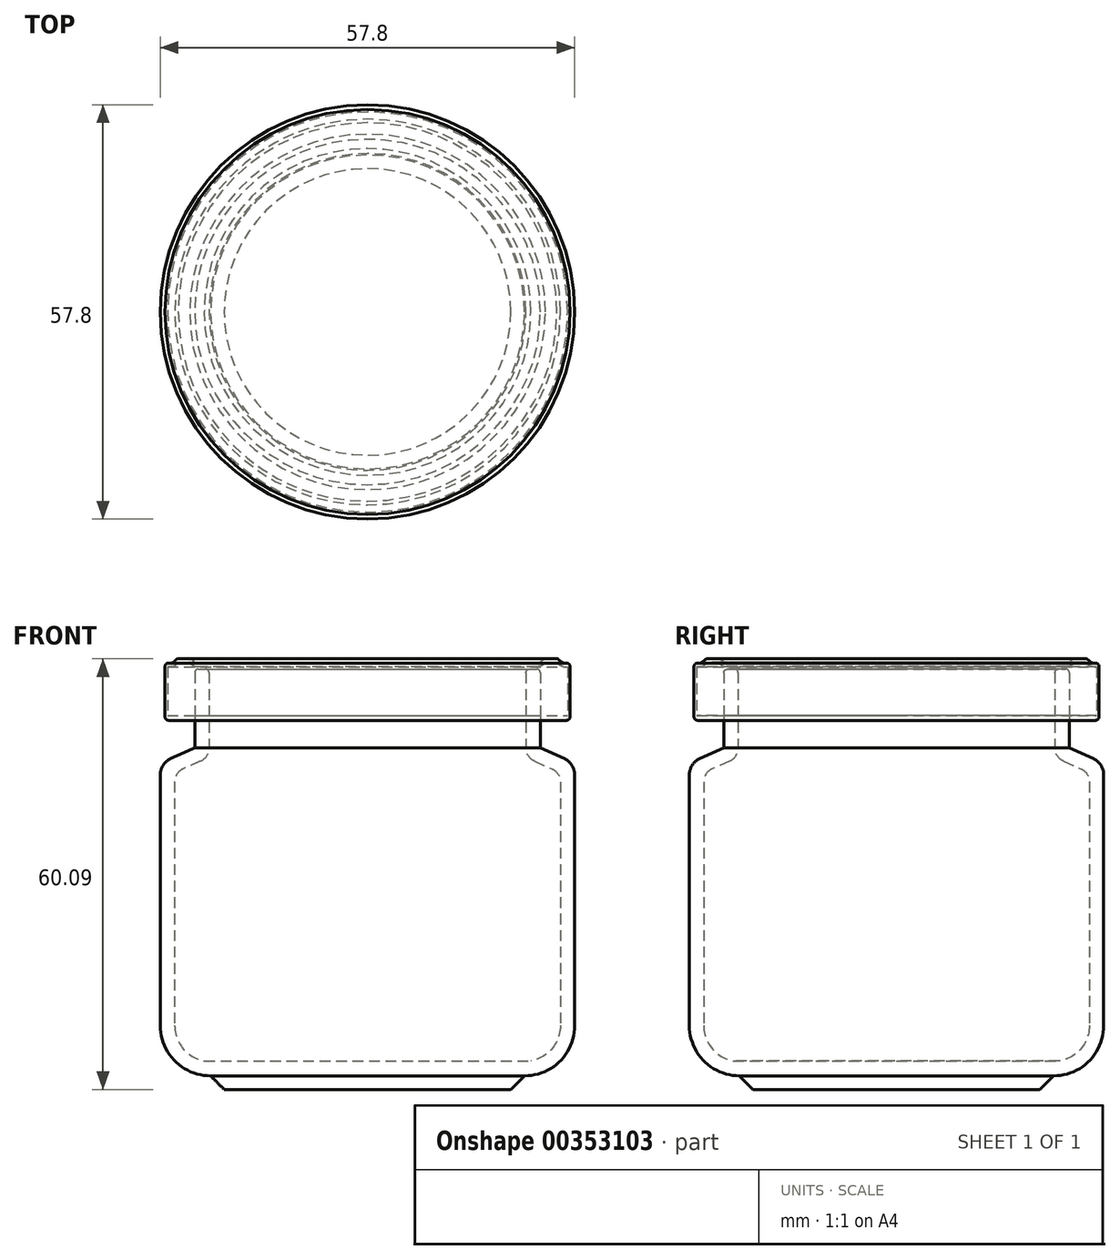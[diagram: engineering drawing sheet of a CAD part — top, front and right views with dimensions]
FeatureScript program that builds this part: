
annotation { "Feature Type Name" : "Feature", "Feature Type Description" : "" }
export const myFeature = defineFeature(function(context is Context, id is Id, definition is map)
    precondition{}
    {
        {
            var Q0;
            Q0=qCreatedBy(makeId("Front.planeOp"),FACE);
            var sketch = newSketch(context, id + "F0", { "sketchPlane" : qUnion([Q0])});
            skLineSegment(sketch, "E0", {"start": v(0, 0) * mm, "end": v(20, 0) * mm});
            skLineSegment(sketch, "E1", {"start": v(20, 0) * mm, "end": v(21.9, 1.9) * mm});
            skArc(sketch, "E2", {"start": v(21.9, 1.9) * mm, "mid": v(26.85, 3.95) * mm, "end": v(28.9, 8.9) * mm});
            skLineSegment(sketch, "E3", {"start": v(28.9, 8.9) * mm, "end": v(28.9, 43.9) * mm});
            skArc(sketch, "E4", {"start": v(28.9, 43.9) * mm, "mid": v(28.5, 45.26) * mm, "end": v(27.41, 46.19) * mm});
            skLineSegment(sketch, "E5", {"start": v(27.41, 46.19) * mm, "end": v(24.1, 47.65) * mm});
            skLineSegment(sketch, "E6", {"start": v(24.1, 47.65) * mm, "end": v(24.1, 58.15) * mm});
            skLineSegment(sketch, "E7.0", {"start": v(22.1, 47.65) * mm, "end": v(22.1, 58.15) * mm});
            skLineSegment(sketch, "E7.1", {"start": v(25.7, 44.75) * mm, "end": v(23.3, 45.82) * mm});
            skLineSegment(sketch, "E7.2", {"start": v(26.9, 8.9) * mm, "end": v(26.9, 42.92) * mm});
            skLineSegment(sketch, "E8", {"start": v(22.6, 58.65) * mm, "end": v(23.6, 58.65) * mm});
            skPoint(sketch, "E9.visualSharp", {"position": v(22.1, 58.65) * mm});
            skArc(sketch, "E9.filletArc", {"start": v(22.6, 58.65) * mm, "mid": v(22.25, 58.5) * mm, "end": v(22.1, 58.15) * mm});
            skPoint(sketch, "E10.visualSharp", {"position": v(24.1, 58.65) * mm});
            skArc(sketch, "E10.filletArc", {"start": v(24.1, 58.15) * mm, "mid": v(23.95, 58.5) * mm, "end": v(23.6, 58.65) * mm});
            skPoint(sketch, "E11.visualSharp", {"position": v(22.1, 46.35) * mm});
            skArc(sketch, "E11.filletArc", {"start": v(22.1, 47.65) * mm, "mid": v(22.42, 46.56) * mm, "end": v(23.3, 45.82) * mm});
            skPoint(sketch, "E12.visualSharp", {"position": v(26.9, 44.23) * mm});
            skArc(sketch, "E12.filletArc", {"start": v(26.9, 42.92) * mm, "mid": v(26.58, 44.01) * mm, "end": v(25.7, 44.75) * mm});
            skPoint(sketch, "E13.visualSharp", {"position": v(26.9, -0.68) * mm});
            skArc(sketch, "E13.filletArc", {"start": v(22.78, 3.98) * mm, "mid": v(25.73, 5.7) * mm, "end": v(26.9, 8.9) * mm});
            skLineSegment(sketch, "E14", {"start": v(22.78, 3.98) * mm, "end": v(0, 3.98) * mm});
            skLineSegment(sketch, "E15", {"start": v(0, 0) * mm, "end": v(0, 55.91) * mm, "construction": true});
            skLineSegment(sketch, "E16", {"start": v(0, 3.98) * mm, "end": v(0, 0) * mm});
            skSolve(sketch);
        }
        {
            var Q0;
            Q0=qCreatedBy(makeId("Front.planeOp"),FACE);
            var sketch = newSketch(context, id + "F1", { "sketchPlane" : qUnion([Q0])});
            skLineSegment(sketch, "E17", {"start": v(24.1, 51.5) * mm, "end": v(27.75, 51.5) * mm});
            skLineSegment(sketch, "E18", {"start": v(28.25, 52) * mm, "end": v(28.25, 59) * mm});
            skLineSegment(sketch, "E19", {"start": v(27.75, 59.5) * mm, "end": v(27.4, 59.5) * mm});
            skLineSegment(sketch, "E20", {"start": v(27.05, 59.65) * mm, "end": v(26.75, 59.95) * mm});
            skLineSegment(sketch, "E21", {"start": v(26.4, 60.1) * mm, "end": v(24.81, 60.1) * mm});
            skLineSegment(sketch, "E22", {"start": v(24.46, 59.95) * mm, "end": v(24.16, 59.65) * mm});
            skLineSegment(sketch, "E23", {"start": v(23.8, 59.5) * mm, "end": v(0, 59.5) * mm});
            skPoint(sketch, "E24.visualSharp", {"position": v(24.01, 59.5) * mm});
            skArc(sketch, "E24.filletArc", {"start": v(23.8, 59.5) * mm, "mid": v(24, 59.54) * mm, "end": v(24.16, 59.65) * mm});
            skPoint(sketch, "E25.visualSharp", {"position": v(24.6, 60.1) * mm});
            skArc(sketch, "E25.filletArc", {"start": v(24.81, 60.1) * mm, "mid": v(24.62, 60.05) * mm, "end": v(24.46, 59.95) * mm});
            skPoint(sketch, "E26.visualSharp", {"position": v(26.6, 60.1) * mm});
            skArc(sketch, "E26.filletArc", {"start": v(26.75, 59.95) * mm, "mid": v(26.59, 60.05) * mm, "end": v(26.4, 60.1) * mm});
            skPoint(sketch, "E27.visualSharp", {"position": v(27.2, 59.5) * mm});
            skArc(sketch, "E27.filletArc", {"start": v(27.05, 59.65) * mm, "mid": v(27.2, 59.54) * mm, "end": v(27.4, 59.5) * mm});
            skPoint(sketch, "E28.visualSharp", {"position": v(28.25, 59.5) * mm});
            skArc(sketch, "E28.filletArc", {"start": v(28.25, 59) * mm, "mid": v(28.1, 59.36) * mm, "end": v(27.75, 59.5) * mm});
            skPoint(sketch, "E29.visualSharp", {"position": v(28.25, 51.5) * mm});
            skArc(sketch, "E29.filletArc", {"start": v(27.75, 51.5) * mm, "mid": v(28.1, 51.65) * mm, "end": v(28.25, 52) * mm});
            skLineSegment(sketch, "E30.0", {"start": v(23.8, 59) * mm, "end": v(0, 59) * mm});
            skArc(sketch, "E30.1", {"start": v(23.8, 59) * mm, "mid": v(24.19, 59.08) * mm, "end": v(24.51, 59.3) * mm});
            skArc(sketch, "E30.2", {"start": v(26.7, 59.3) * mm, "mid": v(26.98, 59.1) * mm, "end": v(27.31, 59) * mm});
            skLineSegment(sketch, "E30.3", {"start": v(26.7, 59.3) * mm, "end": v(26.4, 59.6) * mm});
            skLineSegment(sketch, "E30.4", {"start": v(26.4, 59.6) * mm, "end": v(24.81, 59.6) * mm});
            skLineSegment(sketch, "E30.5", {"start": v(24.81, 59.6) * mm, "end": v(24.51, 59.3) * mm});
            skLineSegment(sketch, "E31", {"start": v(0, 59.5) * mm, "end": v(0, 59) * mm});
            skLineSegment(sketch, "E32", {"start": v(24.1, 51.5) * mm, "end": v(24.1, 52.14) * mm});
            skLineSegment(sketch, "E33", {"start": v(24.1, 52.14) * mm, "end": v(27.9, 52.14) * mm});
            skLineSegment(sketch, "E34", {"start": v(27.9, 52.14) * mm, "end": v(27.9, 58.95) * mm});
            skLineSegment(sketch, "E35", {"start": v(27.9, 58.95) * mm, "end": v(27.31, 59) * mm});
            skSolve(sketch);
        }
        {
            var Q0;
            Q0 = qSketchRegion(id + "F1", true);
            var Q1;
            Q1=sQuery(id+"F0.wireOp",EDGE,"E15");
            revolve(context, id + "F2", {"entities" : qUnion([Q0]), "axis" : qUnion([Q1]), "revolveType" : RevolveType.FULL});
        }
        {
            var Q0;
            Q0 = qSketchRegion(id + "F0", true);
            var Q1;
            Q1=sQuery(id+"F0.wireOp",EDGE,"E15");
            revolve(context, id + "F3", {"entities" : qUnion([Q0]), "axis" : qUnion([Q1]), "revolveType" : RevolveType.FULL});
        }
    });
